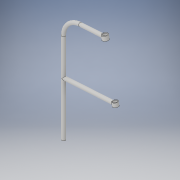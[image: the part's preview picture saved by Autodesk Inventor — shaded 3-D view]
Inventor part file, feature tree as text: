
AUTODESK INVENTOR PART (.ipt)
format: ipt  version: 2018 (Build 220112000, 112)  size: 158,208 bytes
history: native  units: in
note: dims shown in document units (in); Inventor stores cm internally (conversion verified against a paired STEP export)
features: sketch x8, extrude x3, sweep x2, plane x2
ambient origin geometry x8: Origin, YZ Plane, XZ Plane, XY Plane, X Axis, Y Axis, Z Axis, Center Point
bodies: Solid1 (feature_tree)
feature tree (15):
  sweep  "Sweep1"
  sweep  "Sweep2"
  sketch  "Sketch5"  dims[d17=21.5in d18=5.0in]
  plane  "Work Plane1"
  plane  "Work Plane2"
  extrude  "Extrusion1"  Depth=15.0in
  extrude  "Extrusion3"  Depth=15.0in
  extrude  "Extrusion2"  Depth=5.0in
  sketch  "Sketch1"  dims[d1=1.0in d4=0.0in d5=0.0in]
  sketch  "Sketch2"  dims[d6=1.0in d7=0.0in d8=0.0in]
  sketch  "Sketch3"  dims[d13=15.0in d14=19.5in]
  sketch  "Sketch4"  dims[d15=14.5in d16=15.0in]
  sketch  "Sketch6"  dims[d19=14.5in]
  sketch  "Sketch7"  dims[d20=15.0in]
  sketch  "Sketch8"  dims[d21=26.25in d22=1.58in d23=1.15in d24=0.0in d25=1.13in d26=1.0in d27=0.0in d28=1.433in d29=1.027in d30=0.0in d31=20.0in d32=0.0in]
